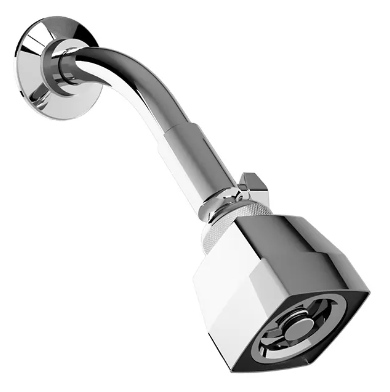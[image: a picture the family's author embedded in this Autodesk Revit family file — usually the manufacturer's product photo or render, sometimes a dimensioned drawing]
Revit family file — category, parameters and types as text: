
# Revit family: AC20-TR011
name_source: partatom
category: Aparatos sanitarios
units: mm (PartAtom-declared; Revit-internal decimal feet)

## family parameters
Activar corte en vistas = No
Compartido = No
Corte con vacíos al cargar = No
Cota de conector redondo = Usar diámetro
Mantener orientación de anotación = No
Número OmniClass = 23.45.00.00
Punto de cálculo de habitación = No
Se basa en plano de trabajo = No
Siempre vertical = Sí
Tipo de pieza = Normal
Título OmniClass = Sanitary, Laundry, and Cleaning Equipment

## types (1)
- AC20-TR011
    Brass Chromed = Brass
    Comentarios de tipo = Showerheads
    Compliance = NOM-008-CONAGUA-1998
    Descripción = Regadera de limpieza automática con válvula de 
control, brazo y chapetón.
    Elevación por defecto = 75"
    Fabricante = HELVEX
    Imagen de tipo = AC20-TR011.png
    Inlet Threads = ½" - 14 NPT
    Max. Working Pressure = 85.3 psi
    Min. Working Pressure = 2.8 psi
    Modelo = AC20-TR011
    Total Length = 11"
    Total Width = 2"
    URL = https://helvex.com.mx

## geometry (parser evidence)
native form markers: Sweep x3
no freeform markers — native parametric forms only
